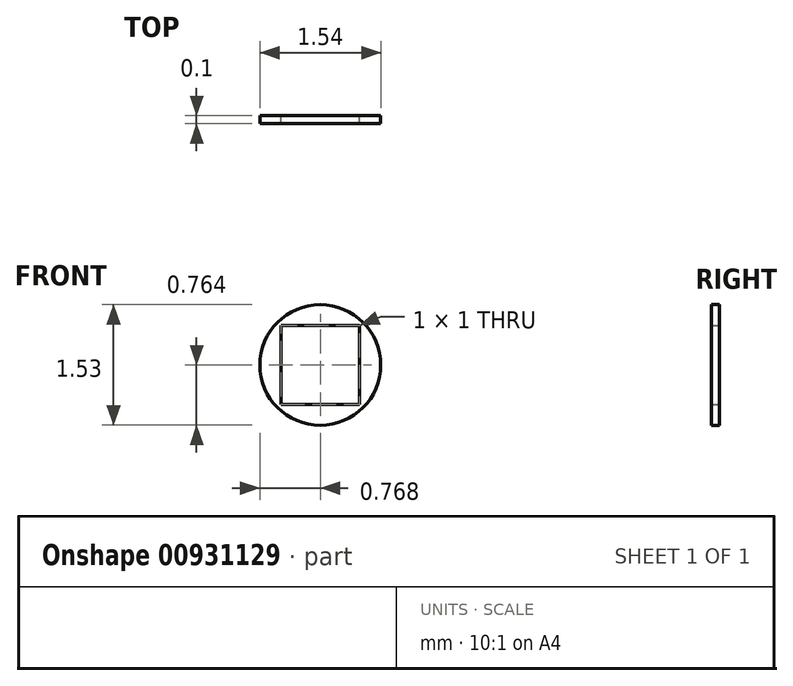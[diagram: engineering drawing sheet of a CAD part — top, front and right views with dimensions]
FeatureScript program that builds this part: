
annotation { "Feature Type Name" : "Feature", "Feature Type Description" : "" }
export const myFeature = defineFeature(function(context is Context, id is Id, definition is map)
    precondition{}
    {
        {
            var Q0;
            Q0=qCreatedBy(makeId("Front.planeOp"),FACE);
            var sketch = newSketch(context, id + "F0", { "sketchPlane" : qUnion([Q0])});
            skLineSegment(sketch, "E0.bottom", {"start": v(-11.42, 42.94) * mm, "end": v(-10.42, 42.94) * mm});
            skLineSegment(sketch, "E0.top", {"start": v(-11.42, 41.94) * mm, "end": v(-10.42, 41.94) * mm});
            skLineSegment(sketch, "E0.left", {"start": v(-11.42, 42.94) * mm, "end": v(-11.42, 41.94) * mm});
            skLineSegment(sketch, "E0.right", {"start": v(-10.42, 42.94) * mm, "end": v(-10.42, 41.94) * mm});
            skLineSegment(sketch, "E1.left", {"start": v(-11.42, 42.94) * mm, "end": v(-11.42, 42.94) * mm});
            skLineSegment(sketch, "E1.right", {"start": v(-10.42, 42.94) * mm, "end": v(-10.42, 42.94) * mm});
            skPoint(sketch, "E2", {"position": v(-10.92, 42.44) * mm});
            skCircle(sketch, "E3", {"center": v(-10.92, 42.44) * mm, "radius": 0.77 * mm});
            skPoint(sketch, "E4", {"position": v(-10.34, 42.95) * mm});
            skSolve(sketch);
        }
        {
            var Q0;
            Q0=makeQuery(id+"F0.imprint","IMPRINT",FACE,{"disambiguationData":[TD([[makeQuery(id+"F0.imprint","IMPRINT",EDGE,{"derivedFrom":sQuery(id+"F0.wireOp",EDGE,"E0.top")}),-1.0]])]});
            extrude(context, id + "F1", {"entities" : qUnion([Q0]), "depth" : 0.1 * mm, "offsetDistance" : 25 * mm});
        }
    });
